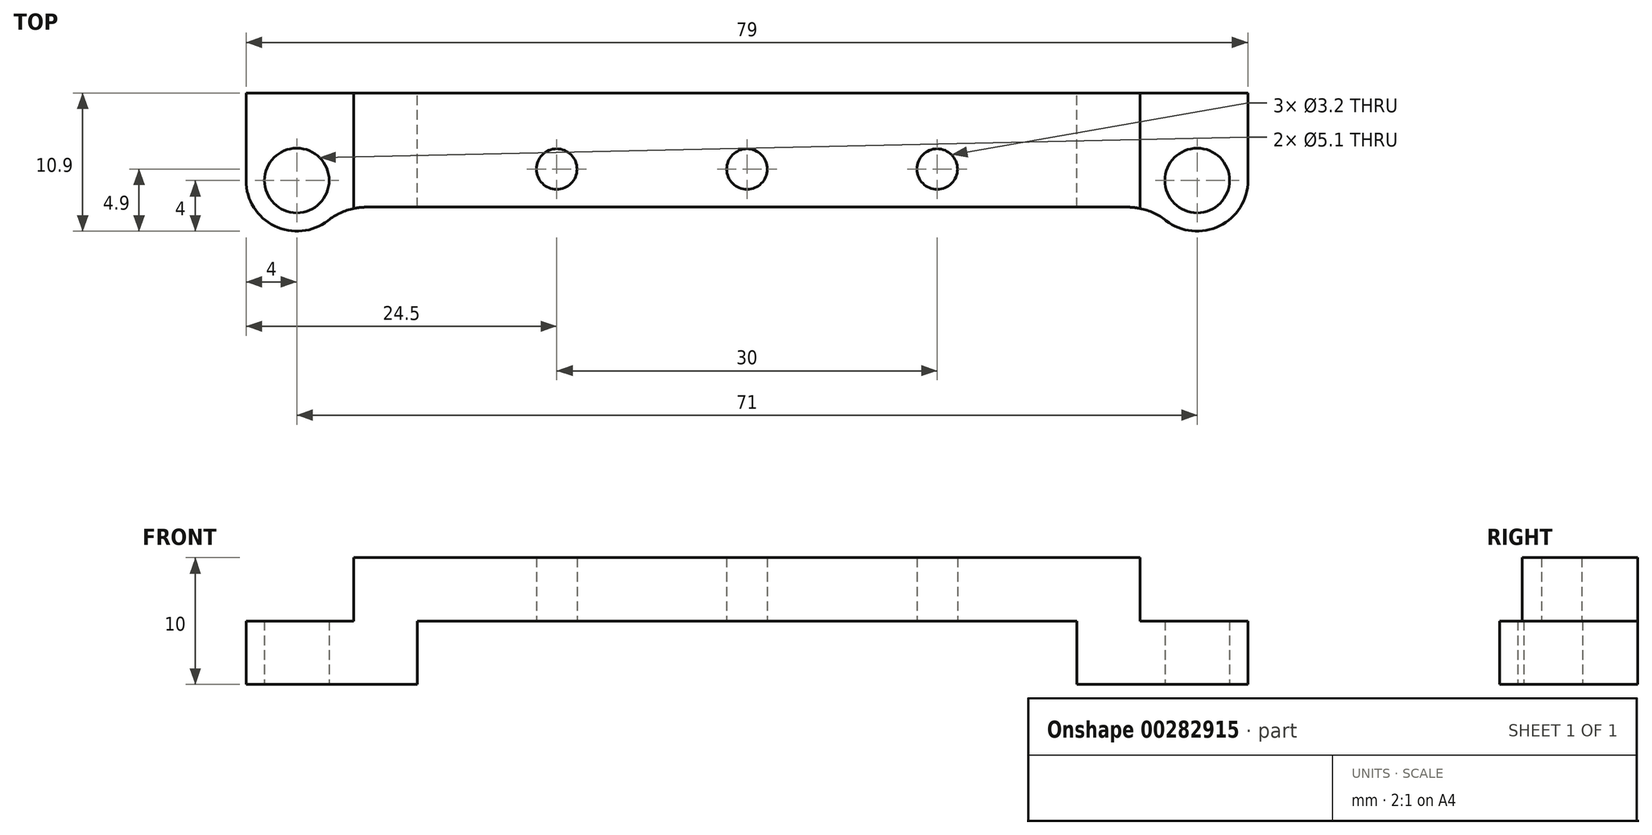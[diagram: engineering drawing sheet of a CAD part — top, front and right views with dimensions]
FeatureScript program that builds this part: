
annotation { "Feature Type Name" : "Feature", "Feature Type Description" : "" }
export const myFeature = defineFeature(function(context is Context, id is Id, definition is map)
    precondition{}
    {
        {
            var Q0;
            Q0=qCreatedBy(makeId("Front.planeOp"),FACE);
            var sketch = newSketch(context, id + "F0", { "sketchPlane" : qUnion([Q0])});
            skLineSegment(sketch, "E0", {"start": v(0, 0) * mm, "end": v(-26, 0) * mm});
            skLineSegment(sketch, "E1", {"start": v(-26, 0) * mm, "end": v(-26, -5) * mm});
            skLineSegment(sketch, "E2", {"start": v(-26, -5) * mm, "end": v(-39.5, -5) * mm});
            skLineSegment(sketch, "E3", {"start": v(-39.5, -5) * mm, "end": v(-39.5, 0) * mm});
            skLineSegment(sketch, "E4", {"start": v(-39.5, 0) * mm, "end": v(-31, 0) * mm});
            skLineSegment(sketch, "E5", {"start": v(-31, 0) * mm, "end": v(-31, 5) * mm});
            skLineSegment(sketch, "E6", {"start": v(-31, 5) * mm, "end": v(0, 5) * mm});
            skLineSegment(sketch, "E7", {"start": v(0, 5) * mm, "end": v(0, 0) * mm});
            skSolve(sketch);
        }
        {
            var Q0;
            Q0=makeQuery(id+"F0.imprint","IMPRINT",FACE,{"disambiguationData":[TD([[makeQuery(id+"F0.imprint","IMPRINT",EDGE,{"derivedFrom":sQuery(id+"F0.wireOp",EDGE,"E0")}),-1.0]])]});
            extrude(context, id + "F1", {"entities" : qUnion([Q0]), "depth" : 10.9 * mm});
        }
        {
            var Q0;
            Q0=makeQuery(id+"F1.opExtrude","SWEPT_FACE",FACE,{"disambiguationData":[OSD([sQuery(id+"F0.wireOp",EDGE,"E2")])]});
            var sketch = newSketch(context, id + "F2", { "sketchPlane" : qUnion([Q0])});
            skArc(sketch, "E8", {"start": v(-32.1, 9) * mm, "mid": v(-36.6, 10.75) * mm, "end": v(-39.5, 6.9) * mm});
            skLineSegment(sketch, "E9", {"start": v(0, 9) * mm, "end": v(-32.1, 9) * mm});
            skLineSegment(sketch, "E10", {"start": v(-39.5, 6.9) * mm, "end": v(-39.5, 12.9) * mm});
            skLineSegment(sketch, "E11", {"start": v(-39.5, 12.9) * mm, "end": v(0, 12.9) * mm});
            skLineSegment(sketch, "E12", {"start": v(0, 12.9) * mm, "end": v(0, 9) * mm});
            skSolve(sketch);
        }
        {
            var Q0;
            Q0 = qSketchRegion(id + "F2", true);
            var Q1;
            Q1=makeQuery(id+"F1.opExtrude","SWEPT_FACE",FACE,{"disambiguationData":[OSD([sQuery(id+"F0.wireOp",EDGE,"E6")])]});
            extrude(context, id + "F3", {"entities" : qUnion([Q0]), "operationType" : NewBodyOperationType.REMOVE, "endBound" : BoundingType.UP_TO_SURFACE, "oppositeDirection" : true, "endBoundEntityFace" : qUnion([Q1]), "depth" : 25 * mm});
        }
        {
            var Q0;
            Q0=makeQuery(id+"F3.boolean.opBoolean","COPY",EDGE,{"derivedFrom":makeQuery(id+"F3.opExtrude","SWEPT_EDGE",EDGE,{"disambiguationData":[OSD([sQuery(id+"F2.wireOp",EDGE,"E8"),sQuery(id+"F2.wireOp",EDGE,"E9")])]})});
            fillet(context, id + "F4", {"entities" : qUnion([Q0]), "radius" : 5 * mm, "tangentPropagation" : true, "allowEdgeOverflow" : false});
        }
        {
            var Q0;
            Q0=makeQuery(id+"F1.opExtrude","SWEPT_FACE",FACE,{"disambiguationData":[OSD([sQuery(id+"F0.wireOp",EDGE,"E2")])]});
            var sketch = newSketch(context, id + "F5", { "sketchPlane" : qUnion([Q0])});
            skArc(sketch, "E13.0", {"start": v(-33.04, 10.06) * mm, "mid": v(-37.26, 10.5) * mm, "end": v(-39.5, 6.9) * mm});
            skSolve(sketch);
        }
        {
            var Q0;
            Q0=sQuery(id+"F5.wireOp",VERTEX,"E13.0.center");
            var Q1;
            Q1=makeQuery(id+"F1.opExtrude","SWEPT_BODY",BODY,{"disambiguationData":[OSD([sQuery(id+"F0.wireOp",EDGE,"E0"),sQuery(id+"F0.wireOp",EDGE,"E1"),sQuery(id+"F0.wireOp",EDGE,"E2"),sQuery(id+"F0.wireOp",EDGE,"E3"),sQuery(id+"F0.wireOp",EDGE,"E4"),sQuery(id+"F0.wireOp",EDGE,"E5"),sQuery(id+"F0.wireOp",EDGE,"E6"),sQuery(id+"F0.wireOp",EDGE,"E7")])]});
            hole(context, id + "F6", {"style" : HoleStyle.SIMPLE, "endStyle" : HoleEndStyle.THROUGH, "holeDiameter" : 5.1 * mm, "tappedDepth" : 12 * mm, "tapClearance" : 3, "locations" : qUnion([Q0]), "scope" : qUnion([Q1])});
        }
        {
            var Q0;
            Q0=makeQuery(id+"F1.opExtrude","SWEPT_BODY",BODY,{"disambiguationData":[OSD([sQuery(id+"F0.wireOp",EDGE,"E0"),sQuery(id+"F0.wireOp",EDGE,"E1"),sQuery(id+"F0.wireOp",EDGE,"E2"),sQuery(id+"F0.wireOp",EDGE,"E3"),sQuery(id+"F0.wireOp",EDGE,"E4"),sQuery(id+"F0.wireOp",EDGE,"E5"),sQuery(id+"F0.wireOp",EDGE,"E6"),sQuery(id+"F0.wireOp",EDGE,"E7")])]});
            var Q1;
            Q1=makeQuery(id+"F1.opExtrude","SWEPT_FACE",FACE,{"disambiguationData":[OSD([sQuery(id+"F0.wireOp",EDGE,"E7")])]});
            mirror(context, id + "F7", {"operationType" : NewBodyOperationType.ADD, "entities" : qUnion([Q0]), "mirrorPlane" : qUnion([Q1])});
        }
        {
            var Q0;
            Q0=qCreatedBy(makeId("Top.planeOp"),FACE);
            var sketch = newSketch(context, id + "F8", { "sketchPlane" : qUnion([Q0])});
            skLineSegment(sketch, "E14.0.0", {"start": v(-26, 0) * mm, "end": v(26, 0) * mm, "construction": true});
            skLineSegment(sketch, "E14.0.1", {"start": v(26, 0) * mm, "end": v(26, -9) * mm, "construction": true});
            skLineSegment(sketch, "E14.0.2", {"start": v(26, -9) * mm, "end": v(-26, -9) * mm, "construction": true});
            skLineSegment(sketch, "E14.0.3", {"start": v(-26, -9) * mm, "end": v(-26, 0) * mm, "construction": true});
            skPoint(sketch, "E15", {"position": v(0, -6) * mm});
            skPoint(sketch, "E16", {"position": v(15, -6) * mm});
            skPoint(sketch, "E17", {"position": v(-15, -6) * mm});
            skSolve(sketch);
        }
        {
            var Q0;
            Q0=sQuery(id+"F8.wireOp",VERTEX,"E17");
            var Q1;
            Q1=sQuery(id+"F8.wireOp",VERTEX,"E15");
            var Q2;
            Q2=sQuery(id+"F8.wireOp",VERTEX,"E16");
            var Q3;
            Q3=makeQuery(id+"F1.opExtrude","SWEPT_BODY",BODY,{"disambiguationData":[OSD([sQuery(id+"F0.wireOp",EDGE,"E0"),sQuery(id+"F0.wireOp",EDGE,"E1"),sQuery(id+"F0.wireOp",EDGE,"E2"),sQuery(id+"F0.wireOp",EDGE,"E3"),sQuery(id+"F0.wireOp",EDGE,"E4"),sQuery(id+"F0.wireOp",EDGE,"E5"),sQuery(id+"F0.wireOp",EDGE,"E6"),sQuery(id+"F0.wireOp",EDGE,"E7")])]});
            hole(context, id + "F9", {"style" : HoleStyle.SIMPLE, "endStyle" : HoleEndStyle.THROUGH, "oppositeDirection" : true, "standardTappedOrClearance" : lookupTablePath({ "standard" : "ISO", "engagement" : "75%", "pitch" : "0.75 mm", "size" : "M4", "type" : "Tapped" }), "standardBlindInLast" : lookupTablePath({ "standard" : "ISO", "engagement" : "75%", "pitch" : "0.75 mm", "size" : "M4", "type" : "Tapped" }), "holeDiameter" : 3.2 * mm, "showTappedDepth" : true, "tappedDepth" : 12 * mm, "tapClearance" : 3, "locations" : qUnion([Q0, Q1, Q2]), "scope" : qUnion([Q3])});
        }
    });
